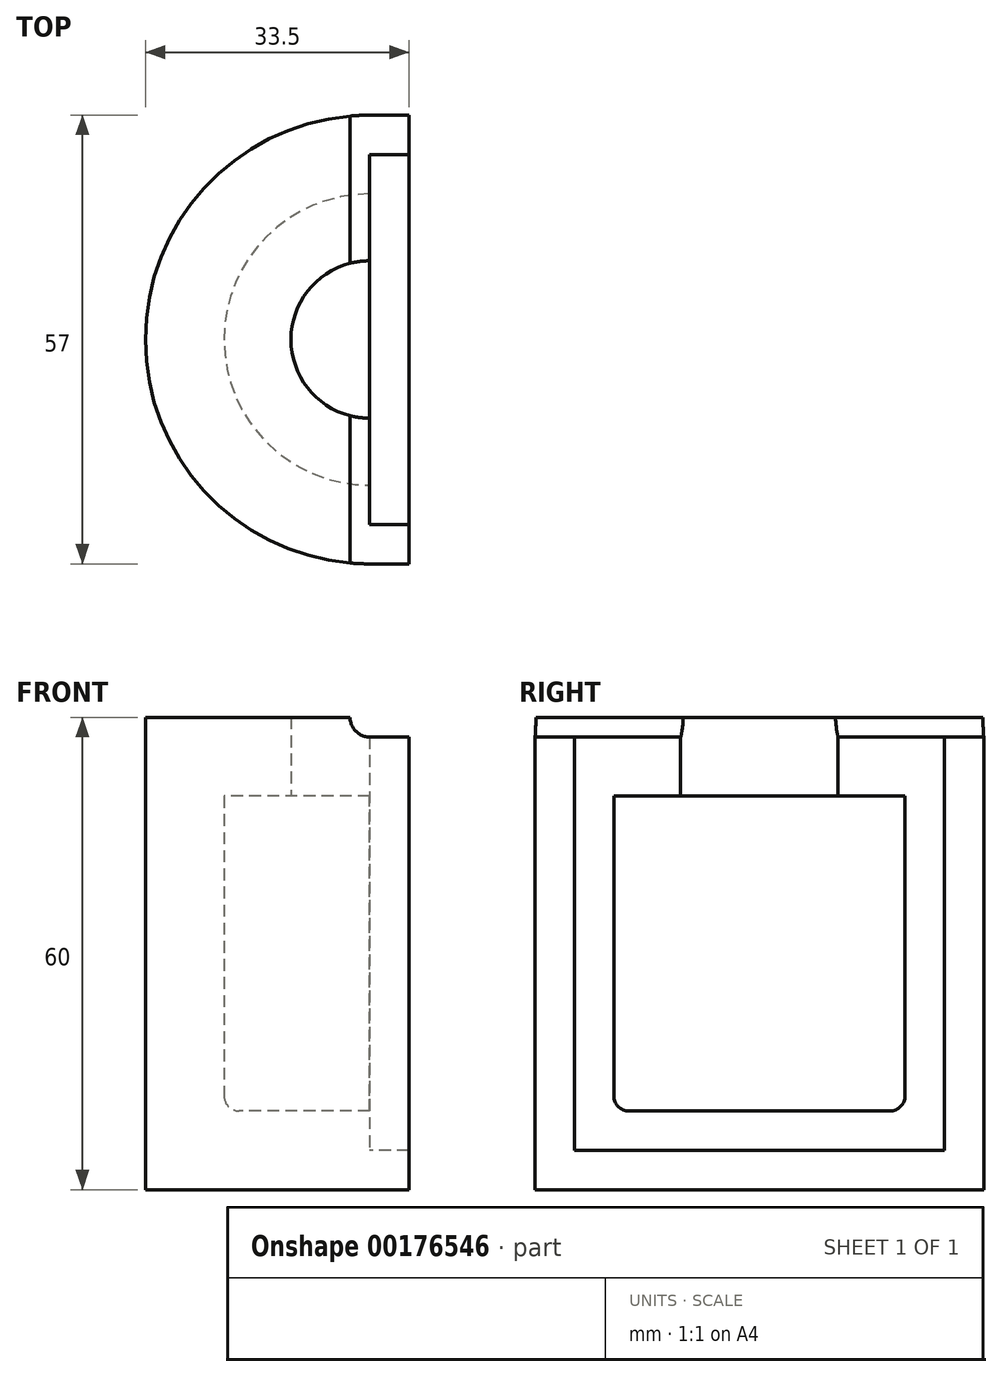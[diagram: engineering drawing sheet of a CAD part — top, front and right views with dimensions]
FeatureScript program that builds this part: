
annotation { "Feature Type Name" : "Feature", "Feature Type Description" : "" }
export const myFeature = defineFeature(function(context is Context, id is Id, definition is map)
    precondition{}
    {
        {
            var Q0;
            Q0=qCreatedBy(makeId("Front.planeOp"),FACE);
            var sketch = newSketch(context, id + "F0", { "sketchPlane" : qUnion([Q0])});
            skLineSegment(sketch, "E0.bottom", {"start": v(0, 0) * mm, "end": v(-18.5, 0) * mm});
            skLineSegment(sketch, "E0.top", {"start": v(0, 10) * mm, "end": v(-18.5, 10) * mm});
            skLineSegment(sketch, "E0.left", {"start": v(0, 0) * mm, "end": v(0, 10) * mm});
            skLineSegment(sketch, "E1.bottom", {"start": v(-18.5, 0) * mm, "end": v(-28.5, 0) * mm});
            skLineSegment(sketch, "E1.top", {"start": v(-18.5, 60) * mm, "end": v(-28.5, 60) * mm});
            skLineSegment(sketch, "E1.left", {"start": v(-18.5, 10) * mm, "end": v(-18.5, 50) * mm});
            skLineSegment(sketch, "E1.right", {"start": v(-28.5, 0) * mm, "end": v(-28.5, 60) * mm});
            skLineSegment(sketch, "E2.bottom", {"start": v(-18.5, 60) * mm, "end": v(-10, 60) * mm});
            skLineSegment(sketch, "E2.top", {"start": v(-18.5, 50) * mm, "end": v(-10, 50) * mm});
            skLineSegment(sketch, "E2.right", {"start": v(-10, 60) * mm, "end": v(-10, 50) * mm});
            skSolve(sketch);
        }
        {
            var Q0;
            Q0=makeQuery(id+"F0.imprint","IMPRINT",FACE,{"disambiguationData":[TD([[makeQuery(id+"F0.imprint","IMPRINT",EDGE,{"derivedFrom":sQuery(id+"F0.wireOp",EDGE,"E0.bottom")}),-1.0]])]});
            var Q1;
            Q1=sQuery(id+"F0.wireOp",EDGE,"E0.left");
            revolve(context, id + "F1", {"entities" : qUnion([Q0]), "axis" : qUnion([Q1]), "revolveType" : RevolveType.SYMMETRIC, "angle" : 180 * degree});
        }
        {
            var Q0;
            Q0=qCreatedBy(makeId("Front.planeOp"),FACE);
            var sketch = newSketch(context, id + "F2", { "sketchPlane" : qUnion([Q0])});
            skLineSegment(sketch, "E3", {"start": v(-28.5, 0) * mm, "end": v(-28.5, 60) * mm});
            skCircle(sketch, "E4", {"center": v(0, 60) * mm, "radius": 2.5 * mm});
            skSolve(sketch);
        }
        {
            var Q0;
            Q0=makeQuery(id+"F2.imprint","IMPRINT",FACE,{"disambiguationData":[TD([[makeQuery(id+"F2.imprint","IMPRINT",EDGE,{"derivedFrom":sQuery(id+"F2.wireOp",EDGE,"E4")}),1.0]])]});
            extrude(context, id + "F3", {"entities" : qUnion([Q0]), "operationType" : NewBodyOperationType.REMOVE, "endBound" : BoundingType.THROUGH_ALL, "oppositeDirection" : true, "depth" : 25.4 * mm, "hasSecondDirection" : true, "secondDirectionBound" : SecondDirectionBoundingType.THROUGH_ALL, "secondDirectionOppositeDirection" : false, "secondDirectionDepth" : 25.4 * mm});
        }
        {
            var Q0;
            Q0=makeQuery(id+"F1.opRevolve","SWEPT_EDGE",EDGE,{"disambiguationData":[OSD([sQuery(id+"F0.wireOp",EDGE,"E0.top"),sQuery(id+"F0.wireOp",EDGE,"E1.left")])]});
            fillet(context, id + "F4", {"entities" : qUnion([Q0]), "radius" : 1.9 * mm, "tangentPropagation" : true, "allowEdgeOverflow" : false});
        }
        {
            var Q0;
            Q0=makeQuery(id+"F1.opRevolve","CAP_FACE",FACE,{"disambiguationData":[OSD([sQuery(id+"F0.wireOp",EDGE,"E0.bottom"),sQuery(id+"F0.wireOp",EDGE,"E0.top"),sQuery(id+"F0.wireOp",EDGE,"E0.left"),sQuery(id+"F0.wireOp",EDGE,"E1.bottom"),sQuery(id+"F0.wireOp",EDGE,"E1.top"),sQuery(id+"F0.wireOp",EDGE,"E1.left"),sQuery(id+"F0.wireOp",EDGE,"E1.right"),sQuery(id+"F0.wireOp",EDGE,"E2.bottom"),sQuery(id+"F0.wireOp",EDGE,"E2.top"),sQuery(id+"F0.wireOp",EDGE,"E2.right")])],"isStart":false});
            var sketch = newSketch(context, id + "F5", { "sketchPlane" : qUnion([Q0])});
            skLineSegment(sketch, "E5", {"start": v(-28.5, 57.5) * mm, "end": v(-28.5, 0) * mm});
            skLineSegment(sketch, "E6", {"start": v(-28.5, 0) * mm, "end": v(28.5, 0) * mm});
            skLineSegment(sketch, "E7", {"start": v(28.5, 0) * mm, "end": v(28.5, 57.5) * mm});
            skLineSegment(sketch, "E8", {"start": v(28.5, 57.5) * mm, "end": v(23.5, 57.5) * mm});
            skLineSegment(sketch, "E9", {"start": v(23.5, 54.5) * mm, "end": v(23.5, 54.5) * mm});
            skLineSegment(sketch, "E10", {"start": v(23.5, 54.5) * mm, "end": v(23.5, 5) * mm});
            skLineSegment(sketch, "E11", {"start": v(23.5, 5) * mm, "end": v(-23.5, 5) * mm});
            skLineSegment(sketch, "E12", {"start": v(-23.5, 5) * mm, "end": v(-23.5, 54.5) * mm});
            skLineSegment(sketch, "E13", {"start": v(-28.5, 57.5) * mm, "end": v(-23.5, 57.5) * mm});
            skLineSegment(sketch, "E14", {"start": v(-23.5, 57.5) * mm, "end": v(-23.5, 54.5) * mm});
            skLineSegment(sketch, "E15", {"start": v(-18.5, 54.5) * mm, "end": v(-23.5, 54.5) * mm});
            skLineSegment(sketch, "E16", {"start": v(-23.5, 54.5) * mm, "end": v(-28.5, 54.5) * mm, "construction": true});
            skLineSegment(sketch, "E17", {"start": v(-23.5, 5) * mm, "end": v(-23.5, 0) * mm, "construction": true});
            skLineSegment(sketch, "E18", {"start": v(23.5, 54.5) * mm, "end": v(28.5, 54.5) * mm, "construction": true});
            skLineSegment(sketch, "E19", {"start": v(23.5, 54.5) * mm, "end": v(23.5, 57.5) * mm});
            skSolve(sketch);
        }
        {
            var Q0;
            Q0=makeQuery(id+"F5.imprint","IMPRINT",FACE,{"disambiguationData":[TD([[makeQuery(id+"F5.imprint","IMPRINT",EDGE,{"derivedFrom":sQuery(id+"F5.wireOp",EDGE,"E5")}),-1.0]])]});
            extrude(context, id + "F6", {"entities" : qUnion([Q0]), "operationType" : NewBodyOperationType.ADD, "depth" : 5 * mm});
        }
    });
